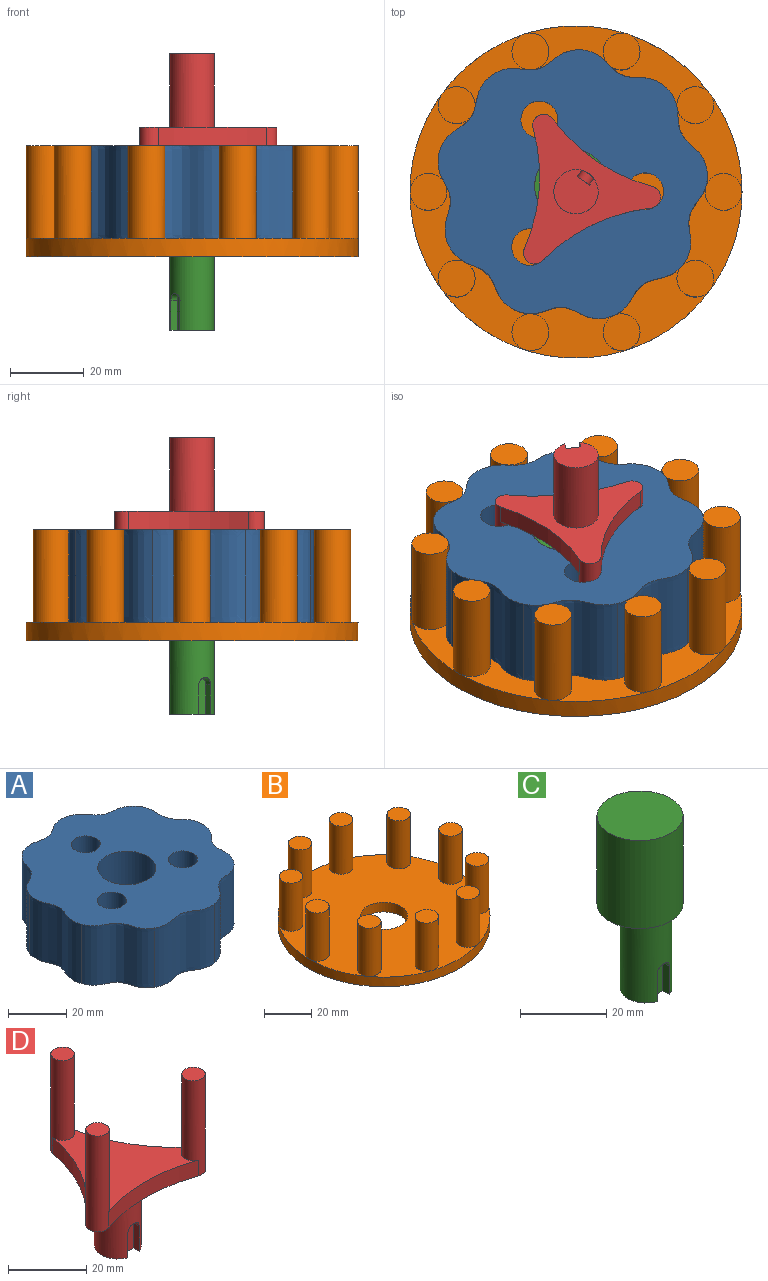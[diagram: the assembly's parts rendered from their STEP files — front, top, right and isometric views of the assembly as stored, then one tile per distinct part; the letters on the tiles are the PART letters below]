
ASSEMBLY  parts=4 mates=3
PART A: 15 faces, bbox 72.4x73.2x25 mm
  f0: extruded ~25x21.92mm, area 648.8mm2, adj f1,f8,f9,f10
  f1: extruded ~25x23.78mm, area 648.8mm2, adj f0,f2,f9,f10
  f2: extruded ~25x23.78mm, area 648.8mm2, adj f1,f3,f9,f10
  f3: extruded ~25x21.92mm, area 648.8mm2, adj f2,f4,f9,f10
  f4: extruded ~25x24.93mm, area 648.8mm2, adj f3,f5,f9,f10
  f5: extruded ~25x19.39mm, area 648.8mm2, adj f4,f6,f9,f10
  f6: extruded ~25.31x25mm, area 648.8mm2, adj f5,f7,f9,f10
  f7: extruded ~25x19.39mm, area 648.8mm2, adj f6,f8,f9,f10
  f8: extruded ~25x24.93mm, area 648.8mm2, adj f0,f7,f9,f10
  f9: plane 73.19x72.37mm, normal (0,0,1), area 3351.3mm2, adj f0,f1,f2,f3,f4,f5,f6,f7
  f10: plane 73.19x72.37mm, normal (0,0,-1), area 3351.3mm2, adj f0,f1,f2,f3,f4,f5,f6,f7
  f11: cylinder r=10mm len=25mm, axis (0,0,-1), area 1570.8mm2, adj f9,f10
  f12: cylinder r=5mm len=25mm, axis (0,0,-1), area 785.4mm2, adj f9,f10
  f13: cylinder r=5mm len=25mm, axis (0,0,-1), area 785.4mm2, adj f9,f10
  f14: cylinder r=5mm len=25mm, axis (0,0,-1), area 785.4mm2, adj f9,f10
PART B: 24 faces, bbox 110x110x50 mm
  f0: cylinder r=10mm len=20mm, axis (0,0,1), area 314.2mm2, adj f2,f3
  f1: cylinder r=45mm len=90mm, axis (0,0,1), area 1413.7mm2, adj f2,f3
  f2: plane 90x90mm, normal (0,0,-1), area 6047.6mm2, adj f0,f1
  f3: plane 90x90mm, normal (0,0,1), area 5262.2mm2, adj f0,f1,f4,f6,f8,f10,f12,f14
  f4: cylinder r=5mm len=25mm, axis (0,0,-1), area 785.4mm2, adj f3,f5
  f5: plane 30x30mm, normal (0,0,1), area 157.1mm2, adj f4
  f6: cylinder r=5mm len=25mm, axis (0,0,-1), area 785.4mm2, adj f3,f7
  f7: plane 10x10mm, normal (0,0,1), area 78.5mm2, adj f6
  f8: cylinder r=5mm len=25mm, axis (0,0,-1), area 785.4mm2, adj f3,f9
  f9: plane 10x10mm, normal (0,0,1), area 78.5mm2, adj f8
  f10: cylinder r=5mm len=25mm, axis (0,0,-1), area 785.4mm2, adj f3,f11
  f11: plane 10x10mm, normal (0,0,1), area 78.5mm2, adj f10
  f12: cylinder r=5mm len=25mm, axis (0,0,-1), area 785.4mm2, adj f3,f13
  f13: plane 10x10mm, normal (0,0,1), area 78.5mm2, adj f12
  f14: cylinder r=5mm len=25mm, axis (0,0,-1), area 785.4mm2, adj f3,f15
  f15: plane 10x10mm, normal (0,0,1), area 78.5mm2, adj f14
  f16: cylinder r=5mm len=25mm, axis (0,0,-1), area 785.4mm2, adj f3,f17
  f17: plane 10x10mm, normal (0,0,1), area 78.5mm2, adj f16
  f18: cylinder r=5mm len=25mm, axis (0,0,-1), area 785.4mm2, adj f3,f19
  f19: plane 10x10mm, normal (0,0,1), area 78.5mm2, adj f18
  f20: cylinder r=5mm len=25mm, axis (0,0,-1), area 785.4mm2, adj f3,f21
  f21: plane 10x10mm, normal (0,0,1), area 78.5mm2, adj f20
  f22: cylinder r=5mm len=25mm, axis (0,0,-1), area 785.4mm2, adj f3,f23
  f23: plane 10x10mm, normal (0,0,1), area 78.5mm2, adj f22
PART C: 9 faces, bbox 20x20x50 mm
  f0: plane 12x11.66mm, normal (0,0,-1), area 103.5mm2, adj f4,f5,f6,f7
  f1: cylinder r=10mm len=25mm, axis (0,0,-1), area 1570.8mm2, adj f2,f3
  f2: plane 20x20mm, normal (0,0,1), area 314.2mm2, adj f1
  f3: plane 20x20mm, normal (0,0,-1), area 201.1mm2, adj f1,f4
  f4: cylinder r=6mm len=25mm, axis (0,0,1), area 903.5mm2, adj f0,f3,f5,f7,f8
  f5: plane 8x2.16mm, normal (1,0,0), area 17.3mm2, adj f0,f4,f6,f8
  f6: plane 10x4mm, normal (0,-1,0), area 38.3mm2, adj f0,f5,f7,f8
  f7: plane 8x2.16mm, normal (-1,0,0), area 17.3mm2, adj f0,f4,f6,f8
  f8: cylinder r=2mm len=4mm, axis (0,1,0), area 14.6mm2, adj f4,f5,f6,f7
PART D: 17 faces, bbox 40.6x36x50 mm
  f0: plane 12x11.66mm, normal (0,0,-1), area 103.5mm2, adj f12,f13,f14,f15
  f1: cylinder r=48.5mm len=28.25mm, axis (0,0,1), area 166.4mm2, adj f2,f6,f7,f8
  f2: cylinder r=3mm len=30mm, axis (0,0,1), area 512.9mm2, adj f1,f3,f7,f8,f9
  f3: cylinder r=48.5mm len=28.25mm, axis (0,0,1), area 166.4mm2, adj f2,f4,f7,f8
  f4: cylinder r=3mm len=30mm, axis (0,0,1), area 512.9mm2, adj f3,f5,f7,f8,f10
  f5: cylinder r=48.5mm len=32.62mm, axis (0,0,1), area 166.4mm2, adj f4,f6,f7,f8
  f6: cylinder r=3mm len=30mm, axis (0,0,1), area 512.9mm2, adj f1,f5,f7,f8,f11
  f7: plane 40.64x36mm, normal (0,0,-1), area 543.7mm2, adj f1,f2,f3,f4,f5,f6,f12
  f8: plane 38.53x33.36mm, normal (0,0,1), area 571.9mm2, adj f1,f2,f3,f4,f5,f6
  f9: plane 6x6mm, normal (0,0,1), area 28.3mm2, adj f2
  f10: plane 6x6mm, normal (0,0,1), area 28.3mm2, adj f4
  f11: plane 6x6mm, normal (0,0,1), area 28.3mm2, adj f6
  f12: cylinder r=6mm len=20mm, axis (0,0,1), area 715mm2, adj f0,f7,f13,f15,f16
  f13: plane 8x2.16mm, normal (1,0,0), area 17.3mm2, adj f0,f12,f14,f16
  f14: plane 10x4mm, normal (0,-1,0), area 38.3mm2, adj f0,f13,f15,f16
  f15: plane 8x2.16mm, normal (-1,0,0), area 17.3mm2, adj f0,f12,f14,f16
  f16: cylinder r=2mm len=4mm, axis (0,1,0), area 14.6mm2, adj f12,f13,f14,f15
PLACE A rot(axis=(0.96,-0.29,0),180deg) t=(-1.21,1.59,30)mm
PLACE B t=(0,0,5)mm fixed
PLACE C rot(axis=(0,0,-1),52.8deg) t=(-1.21,1.59,5)mm
PLACE D rot(axis=(-0.96,0.29,0),180deg) t=(0,0,30)mm
MATE revolute C.f4 <-> B.f1  axis (0,0,-1) through (0,0,5)mm
MATE revolute D.f12 <-> B.f1  axis (0,0,-1) through (0,0,30)mm
MATE revolute A.f11 <-> C.f1  axis (0,0,1) through (-1.21,1.59,30)mm
